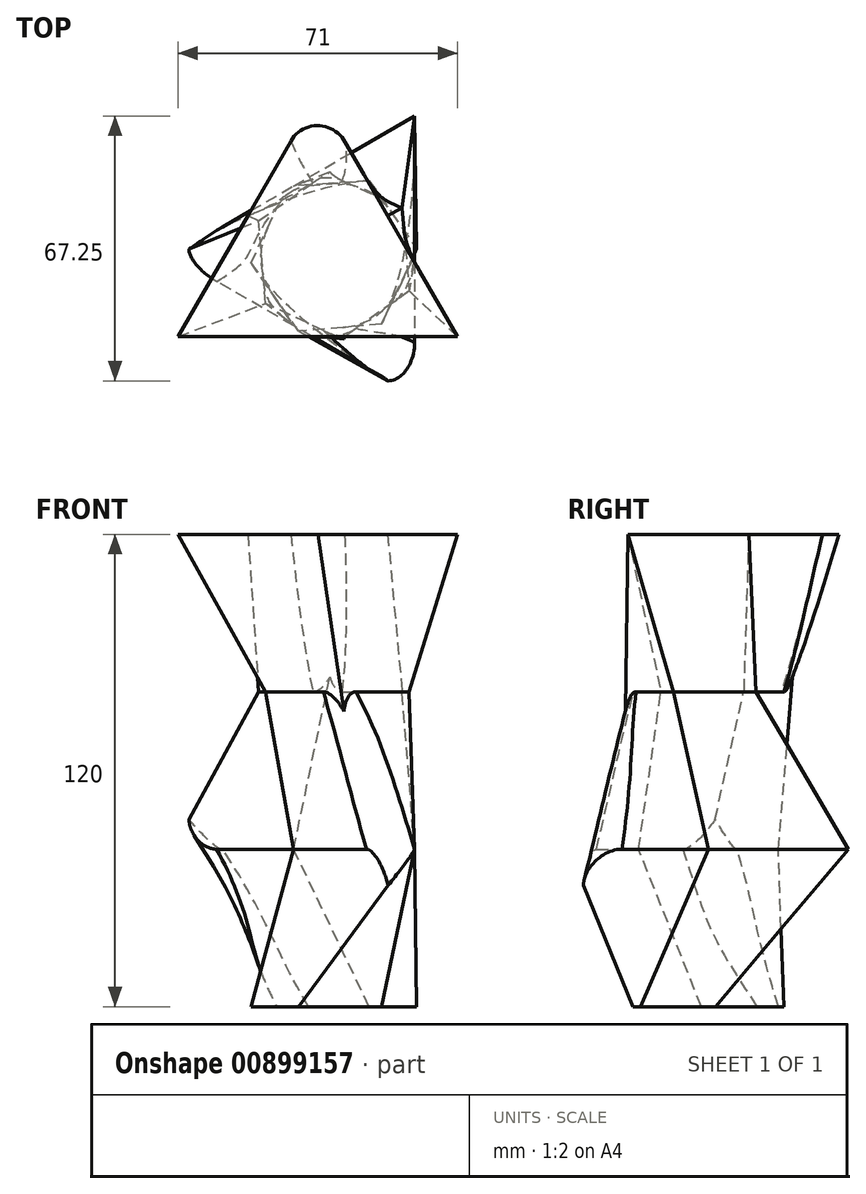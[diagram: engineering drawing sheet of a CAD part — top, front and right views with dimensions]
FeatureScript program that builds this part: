
annotation { "Feature Type Name" : "Feature", "Feature Type Description" : "" }
export const myFeature = defineFeature(function(context is Context, id is Id, definition is map)
    precondition{}
    {
        {
            var Q0;
            Q0=qCreatedBy(makeId("Top.planeOp"),FACE);
            var sketch = newSketch(context, id + "F0", { "sketchPlane" : qUnion([Q0])});
            skCircle(sketch, "E0.cCircle", {"center": v(0, 0) * mm, "radius": 18.29 * mm, "construction": true});
            skLineSegment(sketch, "E0.0", {"start": v(-8.95, -19.13) * mm, "end": v(-21.04, -1.8) * mm});
            skLineSegment(sketch, "E0.1", {"start": v(-21.04, -1.8) * mm, "end": v(-12.09, 17.32) * mm});
            skLineSegment(sketch, "E0.2", {"start": v(-12.09, 17.32) * mm, "end": v(8.95, 19.13) * mm});
            skLineSegment(sketch, "E0.3", {"start": v(8.95, 19.13) * mm, "end": v(21.04, 1.8) * mm});
            skLineSegment(sketch, "E0.4", {"start": v(21.04, 1.8) * mm, "end": v(12.09, -17.32) * mm});
            skLineSegment(sketch, "E0.5", {"start": v(12.09, -17.32) * mm, "end": v(-8.95, -19.13) * mm});
            skPoint(sketch, "E0.0.midPoint", {"position": v(-15, -10.47) * mm});
            skSolve(sketch);
        }
        {
            var Q0;
            Q0=qCreatedBy(makeId("Top.planeOp"),FACE);
            cPlane(context, id + "F1", {"entities" : qUnion([Q0]), "cplaneType" : CPlaneType.OFFSET, "offset" : 40 * mm, "width" : 150 * mm, "height" : 150 * mm});
        }
        {
            var Q0;
            Q0=qCreatedBy(id+"F1.planeOp",FACE);
            var sketch = newSketch(context, id + "F2", { "sketchPlane" : qUnion([Q0])});
            skCircle(sketch, "E1.cCircle", {"center": v(0, 0) * mm, "radius": 20.5 * mm, "construction": true});
            skLineSegment(sketch, "E1.0", {"start": v(20.5, 35.5) * mm, "end": v(20.5, -35.5) * mm});
            skLineSegment(sketch, "E1.1", {"start": v(20.5, -35.5) * mm, "end": v(-41, 0) * mm});
            skLineSegment(sketch, "E1.2", {"start": v(-41, 0) * mm, "end": v(20.5, 35.5) * mm});
            skPoint(sketch, "E1.0.midPoint", {"position": v(20.5, 0) * mm});
            skSolve(sketch);
        }
        {
            var Q0;
            Q0=qCreatedBy(makeId("Top.planeOp"),FACE);
            cPlane(context, id + "F3", {"entities" : qUnion([Q0]), "cplaneType" : CPlaneType.OFFSET, "offset" : 80 * mm, "width" : 150 * mm, "height" : 150 * mm});
        }
        {
            var Q0;
            Q0=qCreatedBy(id+"F3.planeOp",FACE);
            var sketch = newSketch(context, id + "F4", { "sketchPlane" : qUnion([Q0])});
            skCircle(sketch, "E2.cCircle", {"center": v(0, 0) * mm, "radius": 18.29 * mm, "construction": true});
            skLineSegment(sketch, "E2.0", {"start": v(-19.13, 8.95) * mm, "end": v(-1.8, 21.04) * mm});
            skLineSegment(sketch, "E2.1", {"start": v(-1.8, 21.04) * mm, "end": v(17.32, 12.09) * mm});
            skLineSegment(sketch, "E2.2", {"start": v(17.32, 12.09) * mm, "end": v(19.13, -8.95) * mm});
            skLineSegment(sketch, "E2.3", {"start": v(19.13, -8.95) * mm, "end": v(1.8, -21.04) * mm});
            skLineSegment(sketch, "E2.4", {"start": v(1.8, -21.04) * mm, "end": v(-17.32, -12.09) * mm});
            skLineSegment(sketch, "E2.5", {"start": v(-17.32, -12.09) * mm, "end": v(-19.13, 8.95) * mm});
            skPoint(sketch, "E2.0.midPoint", {"position": v(-10.47, 15) * mm});
            skSolve(sketch);
        }
        {
            var Q0;
            Q0=qCreatedBy(makeId("Top.planeOp"),FACE);
            cPlane(context, id + "F5", {"entities" : qUnion([Q0]), "cplaneType" : CPlaneType.OFFSET, "offset" : 120 * mm, "width" : 150 * mm, "height" : 150 * mm});
        }
        {
            var Q0;
            Q0=qCreatedBy(id+"F5.planeOp",FACE);
            var sketch = newSketch(context, id + "F6", { "sketchPlane" : qUnion([Q0])});
            skCircle(sketch, "E3.cCircle", {"center": v(-4.1, 0) * mm, "radius": 20.5 * mm, "construction": true});
            skLineSegment(sketch, "E3.0", {"start": v(31.4, -20.5) * mm, "end": v(-39.6, -20.5) * mm});
            skLineSegment(sketch, "E3.1", {"start": v(-39.6, -20.5) * mm, "end": v(-4.1, 41) * mm});
            skLineSegment(sketch, "E3.2", {"start": v(-4.1, 41) * mm, "end": v(31.4, -20.5) * mm});
            skPoint(sketch, "E3.0.midPoint", {"position": v(-4.1, -20.5) * mm});
            skSolve(sketch);
        }
        {
            var Q0;
            Q0 = qSketchRegion(id + "F0", true);
            var Q1;
            Q1 = qSketchRegion(id + "F2", true);
            loft(context, id + "F7", {"sheetProfilesArray" : [{ "sheetProfileEntities" : qUnion([Q0]) }, { "sheetProfileEntities" : qUnion([Q1]) }]});
        }
        {
            var Q1;
            Q1 = qSketchRegion(id + "F2", true);
            var Q2;
            Q2 = qSketchRegion(id + "F4", true);
            loft(context, id + "F8", {"operationType" : NewBodyOperationType.ADD, "sheetProfilesArray" : [{ "sheetProfileEntities" : qUnion([Q1]) }, { "sheetProfileEntities" : qUnion([Q2]) }]});
        }
        {
            var Q1;
            Q1 = qSketchRegion(id + "F6", true);
            var Q2;
            Q2 = qSketchRegion(id + "F4", true);
            loft(context, id + "F9", {"operationType" : NewBodyOperationType.ADD, "sheetProfilesArray" : [{ "sheetProfileEntities" : qUnion([Q1]) }, { "sheetProfileEntities" : qUnion([Q2]) }]});
        }
        {
            var Q0;
            Q0=makeQuery(id+"F9.opLoft","SWEPT_EDGE",EDGE,{"disambiguationData":[OSD([sQuery(id+"F4.wireOp",EDGE,"E2.0"),sQuery(id+"F4.wireOp",EDGE,"E2.1"),sQuery(id+"F6.wireOp",EDGE,"E3.0"),sQuery(id+"F6.wireOp",EDGE,"E3.2")])]});
            var Q1;
            Q1=makeQuery(id+"F8.opLoft","SWEPT_EDGE",EDGE,{"disambiguationData":[OSD([sQuery(id+"F2.wireOp",EDGE,"E1.0"),sQuery(id+"F2.wireOp",EDGE,"E1.1"),sQuery(id+"F4.wireOp",EDGE,"E2.2"),sQuery(id+"F4.wireOp",EDGE,"E2.3")])]});
            var Q2;
            Q2=makeQuery(id+"F7.opLoft","SWEPT_EDGE",EDGE,{"disambiguationData":[OSD([sQuery(id+"F0.wireOp",EDGE,"E0.0"),sQuery(id+"F0.wireOp",EDGE,"E0.1"),sQuery(id+"F2.wireOp",EDGE,"E1.1"),sQuery(id+"F2.wireOp",EDGE,"E1.2")])]});
            fillet(context, id + "F10", {"entities" : qUnion([Q0, Q1, Q2]), "radius" : 8 * mm, "tangentPropagation" : true, "allowEdgeOverflow" : false});
        }
    });
